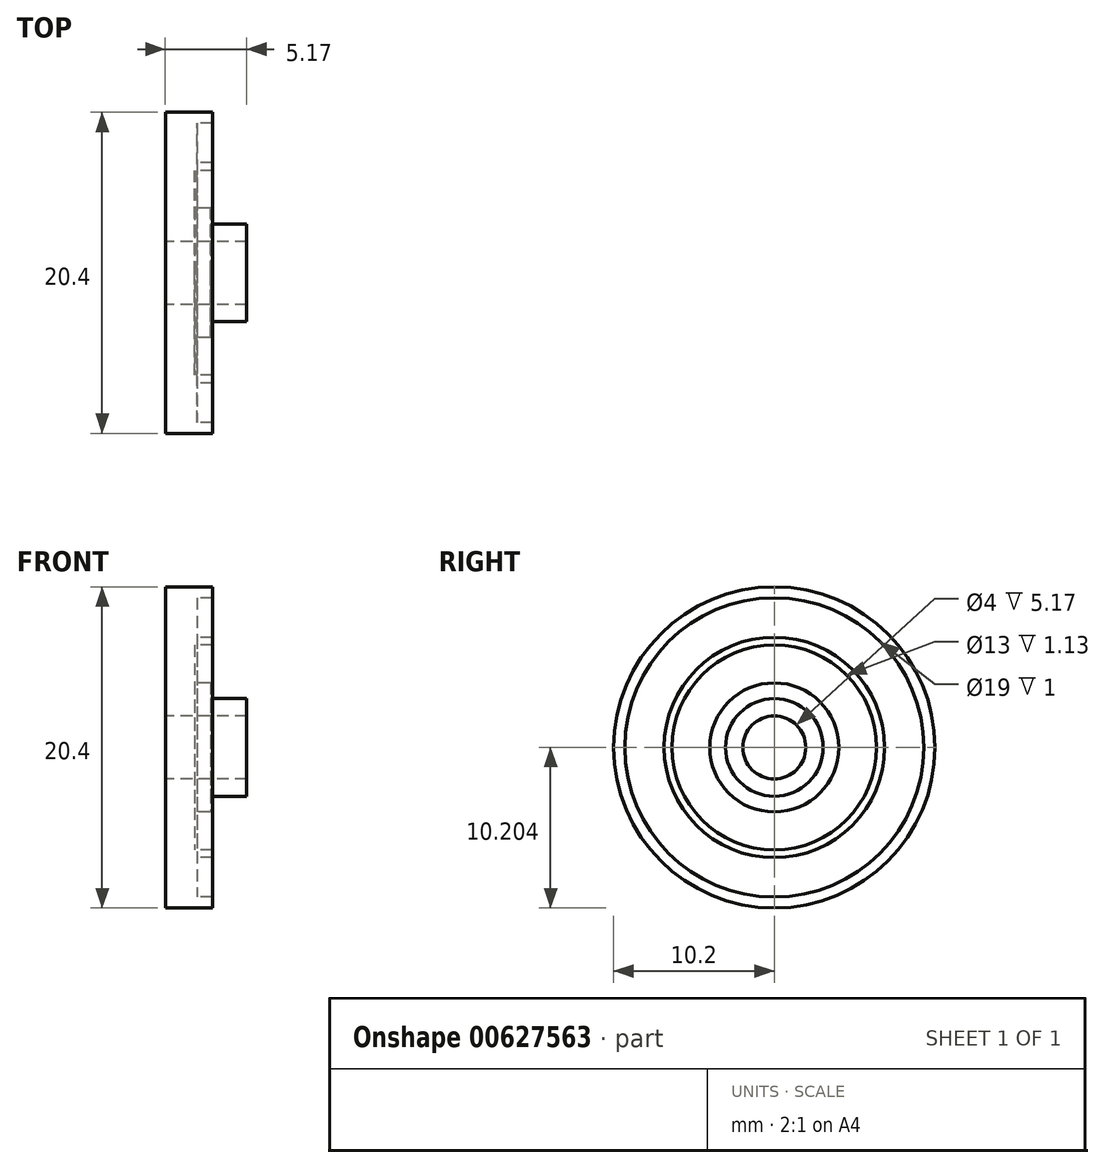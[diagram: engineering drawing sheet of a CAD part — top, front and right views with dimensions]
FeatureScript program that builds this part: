
annotation { "Feature Type Name" : "Feature", "Feature Type Description" : "" }
export const myFeature = defineFeature(function(context is Context, id is Id, definition is map)
    precondition{}
    {
        {
            var Q0;
            Q0=qCreatedBy(makeId("Front.planeOp"),FACE);
            var sketch = newSketch(context, id + "F0", { "sketchPlane" : qUnion([Q0])});
            skLineSegment(sketch, "E0", {"start": v(-10.04, 7.96) * mm, "end": v(-10.04, -0.24) * mm});
            skLineSegment(sketch, "E1", {"start": v(-10.04, -0.24) * mm, "end": v(-4.87, -0.24) * mm});
            skLineSegment(sketch, "E2", {"start": v(-4.87, -0.24) * mm, "end": v(-4.87, 0.86) * mm});
            skLineSegment(sketch, "E3", {"start": v(-4.87, 0.86) * mm, "end": v(-7.17, 0.86) * mm});
            skLineSegment(sketch, "E4", {"start": v(-7.17, 0.86) * mm, "end": v(-7.17, 1.86) * mm});
            skLineSegment(sketch, "E5", {"start": v(-7.17, 1.86) * mm, "end": v(-8.17, 1.86) * mm});
            skLineSegment(sketch, "E6", {"start": v(-8.17, 1.86) * mm, "end": v(-8.17, 4.26) * mm});
            skLineSegment(sketch, "E7", {"start": v(-8.17, 4.26) * mm, "end": v(-7.04, 4.26) * mm});
            skLineSegment(sketch, "E8", {"start": v(-7.04, 4.26) * mm, "end": v(-7.04, 4.76) * mm});
            skLineSegment(sketch, "E9", {"start": v(-7.04, 4.76) * mm, "end": v(-8.04, 4.76) * mm});
            skLineSegment(sketch, "E10", {"start": v(-8.04, 4.76) * mm, "end": v(-8.04, 7.26) * mm});
            skLineSegment(sketch, "E11", {"start": v(-8.04, 7.26) * mm, "end": v(-7.04, 7.26) * mm});
            skLineSegment(sketch, "E12", {"start": v(-7.04, 7.26) * mm, "end": v(-7.04, 7.96) * mm});
            skLineSegment(sketch, "E13", {"start": v(-7.04, 7.96) * mm, "end": v(-10.04, 7.96) * mm});
            skLineSegment(sketch, "E14", {"start": v(-12.93, -2.24) * mm, "end": v(-0.6, -2.24) * mm, "construction": true});
            skSolve(sketch);
        }
        {
            var Q0;
            Q0=makeQuery(id+"F0.imprint","IMPRINT",FACE,{"disambiguationData":[TD([[makeQuery(id+"F0.imprint","IMPRINT",EDGE,{"derivedFrom":sQuery(id+"F0.wireOp",EDGE,"E0")}),1.0]])]});
            var Q1;
            Q1=sQuery(id+"F0.wireOp",EDGE,"E14");
            revolve(context, id + "F1", {"entities" : qUnion([Q0]), "axis" : qUnion([Q1]), "revolveType" : RevolveType.FULL});
        }
    });
